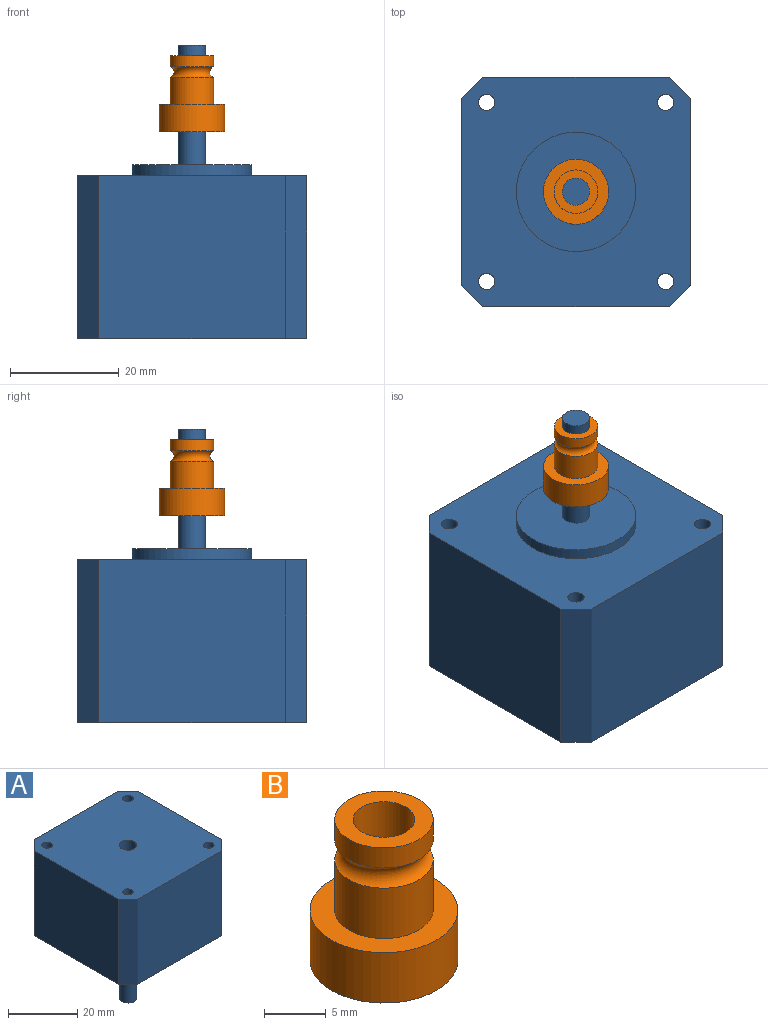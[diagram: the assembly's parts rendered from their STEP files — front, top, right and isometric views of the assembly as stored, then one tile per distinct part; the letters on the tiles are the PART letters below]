
ASSEMBLY  parts=2 mates=1
PART A: 20 faces, bbox 42.3x42.3x54 mm
  f0: plane 34.3x30mm, normal (1,0,0), area 1029mm2, adj f9,f10,f18,f19
  f1: plane 34.3x30mm, normal (0,1,0), area 1029mm2, adj f9,f10,f16,f19
  f2: plane 34.3x30mm, normal (-1,0,0), area 1029mm2, adj f9,f10,f16,f17
  f3: cylinder r=1.5mm len=30mm, axis (0,0,-1), area 282.7mm2, adj f9,f10
  f4: cylinder r=1.5mm len=30mm, axis (0,0,-1), area 282.7mm2, adj f9,f10
  f5: cylinder r=1.5mm len=30mm, axis (0,0,-1), area 282.7mm2, adj f9,f10
  f6: cylinder r=1.5mm len=30mm, axis (0,0,-1), area 282.7mm2, adj f9,f10
  f7: plane 34.3x30mm, normal (0,-1,0), area 1029mm2, adj f9,f10,f17,f18
  f8: cylinder r=2.5mm len=30mm, axis (0,0,-1), area 471.2mm2, adj f9,f15
  f9: plane 42.3x42.3mm, normal (0,0,1), area 1709.4mm2, adj f0,f1,f2,f3,f4,f5,f6,f7
  f10: plane 42.3x42.3mm, normal (0,0,-1), area 1348.9mm2, adj f0,f1,f2,f3,f4,f5,f6,f7
  f11: cylinder r=11mm len=22mm, axis (0,0,1), area 138.2mm2, adj f10,f12
  f12: plane 22x22mm, normal (0,0,-1), area 360.5mm2, adj f11,f14
  f13: plane 5x5mm, normal (0,0,-1), area 19.6mm2, adj f14
  f14: cylinder r=2.5mm len=22mm, axis (0,0,1), area 345.6mm2, adj f12,f13
  f15: plane 5x5mm, normal (0,0,1), area 19.6mm2, adj f8
  f16: plane 30x4mm, normal (-0.71,0.71,0), area 169.7mm2, adj f1,f2,f9,f10
  f17: plane 30x4mm, normal (-0.71,-0.71,0), area 169.7mm2, adj f2,f7,f9,f10
  f18: plane 30x4mm, normal (0.71,-0.71,0), area 169.7mm2, adj f0,f7,f9,f10
  f19: plane 30x4mm, normal (0.71,0.71,0), area 169.7mm2, adj f0,f1,f9,f10
PART B: 8 faces, bbox 12x12x14 mm
  f0: plane 12x12mm, normal (0,0,-1), area 93.5mm2, adj f1,f7
  f1: cylinder r=6mm len=12mm, axis (0,0,-1), area 188.5mm2, adj f0,f2
  f2: plane 12x12mm, normal (0,0,1), area 62.8mm2, adj f1,f3
  f3: cylinder r=4mm len=8mm, axis (0,0,-1), area 125.7mm2, adj f2,f4
  f4: torus R=4.36mm, axis (0,0,-1), area 57.9mm2, adj f3,f5
  f5: cylinder r=4mm len=8mm, axis (0,0,-1), area 50.3mm2, adj f4,f6
  f6: plane 8x8mm, normal (0,0,1), area 30.6mm2, adj f5,f7
  f7: cylinder r=2.5mm len=14mm, axis (0,0,1), area 219.9mm2, adj f0,f6
PLACE A rot(axis=(1,0,0),180deg) t=(-13.47,6.7,13.39)mm
PLACE B t=(-13.47,6.7,21.51)mm
MATE slider B.f7 <-> A.f8  axis (0,0,1) through (-13.47,6.7,35.51)mm
